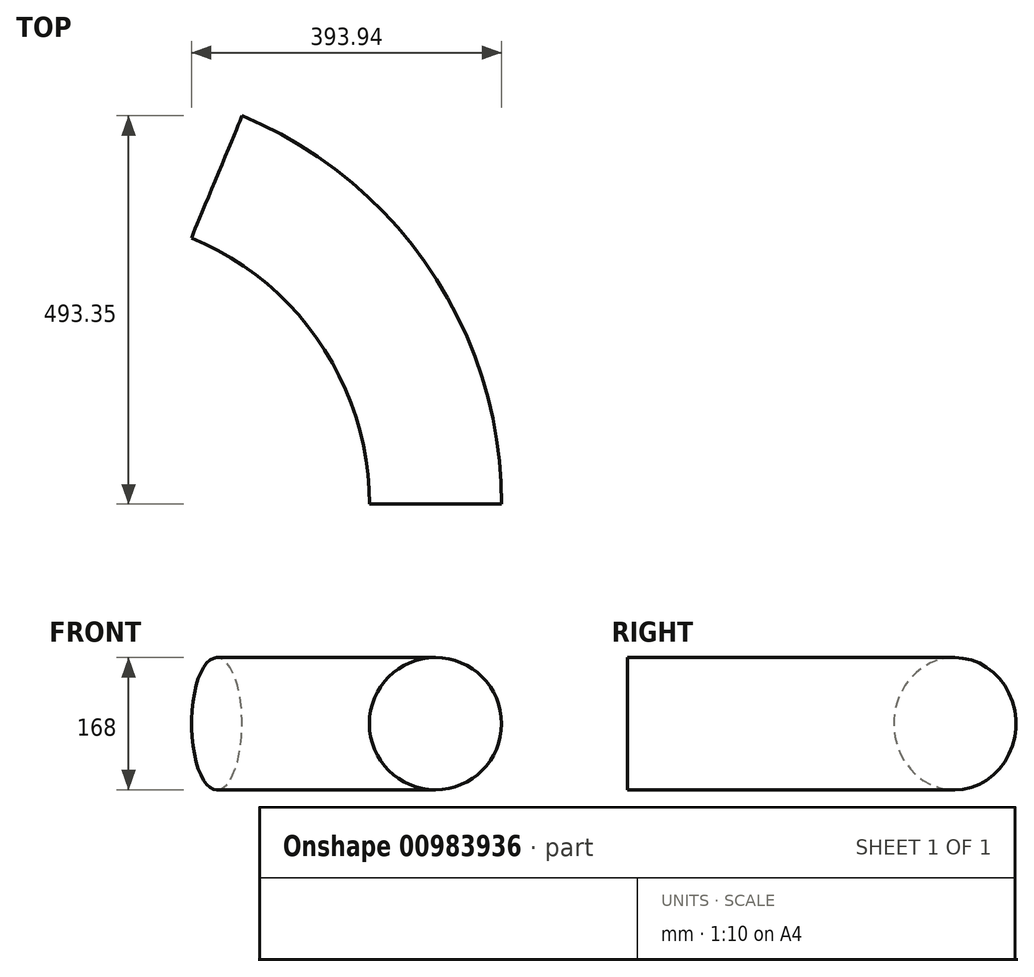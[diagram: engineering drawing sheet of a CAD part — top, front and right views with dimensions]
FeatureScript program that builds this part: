
annotation { "Feature Type Name" : "Feature", "Feature Type Description" : "" }
export const myFeature = defineFeature(function(context is Context, id is Id, definition is map)
    precondition{}
    {
        {
            var Q0;
            Q0=qCreatedBy(makeId("Top.planeOp"),FACE);
            var sketch = newSketch(context, id + "F0", { "sketchPlane" : qUnion([Q0])});
            skArc(sketch, "E0", {"start": v(450, 0) * mm, "mid": v(374.16, 250) * mm, "end": v(172.2, 415.75) * mm});
            skSolve(sketch);
        }
        {
            var Q0;
            Q0=qCreatedBy(makeId("Front.planeOp"),FACE);
            var sketch = newSketch(context, id + "F1", { "sketchPlane" : qUnion([Q0])});
            skCircle(sketch, "E1", {"center": v(450, 0) * mm, "radius": 84 * mm});
            skSolve(sketch);
        }
        {
            var Q0;
            Q0=makeQuery(id+"F1.imprint","IMPRINT",FACE,{"disambiguationData":[TD([[makeQuery(id+"F1.imprint","IMPRINT",EDGE,{"derivedFrom":sQuery(id+"F1.wireOp",EDGE,"E1")}),1.0]])]});
            var Q1;
            Q1=sQuery(id+"F0.wireOp",EDGE,"E0");
            sweep(context, id + "F2", {"profiles" : qUnion([Q0]), "path" : qUnion([Q1])});
        }
    });
